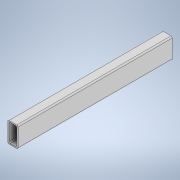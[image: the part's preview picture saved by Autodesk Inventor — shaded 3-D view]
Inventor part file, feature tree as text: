
AUTODESK INVENTOR PART (.ipt)
format: ipt  version: 2020 (Build 240168000, 168)  size: 126,976 bytes
history: native  units: in
note: dims shown in document units (in); Inventor stores cm internally (conversion verified against a paired STEP export)
features: extrude x1, sketch x1
ambient origin geometry x8: Origin, YZ Plane, XZ Plane, XY Plane, X Axis, Y Axis, Z Axis, Center Point
bodies: Solid1 (feature_tree)
feature tree (2):
  extrude  "Extrusion1"  Depth=1.0in
  sketch  "Sketch1"  dims[d0=2.0in d1=1.0in d2=0.125in d3=0.125in d4=0.125in d5=0.125in d6=0.125in d7=0.125in d8=0.125in d9=0.125in d10=0.125in d11=15.0in d12=0.0in]
